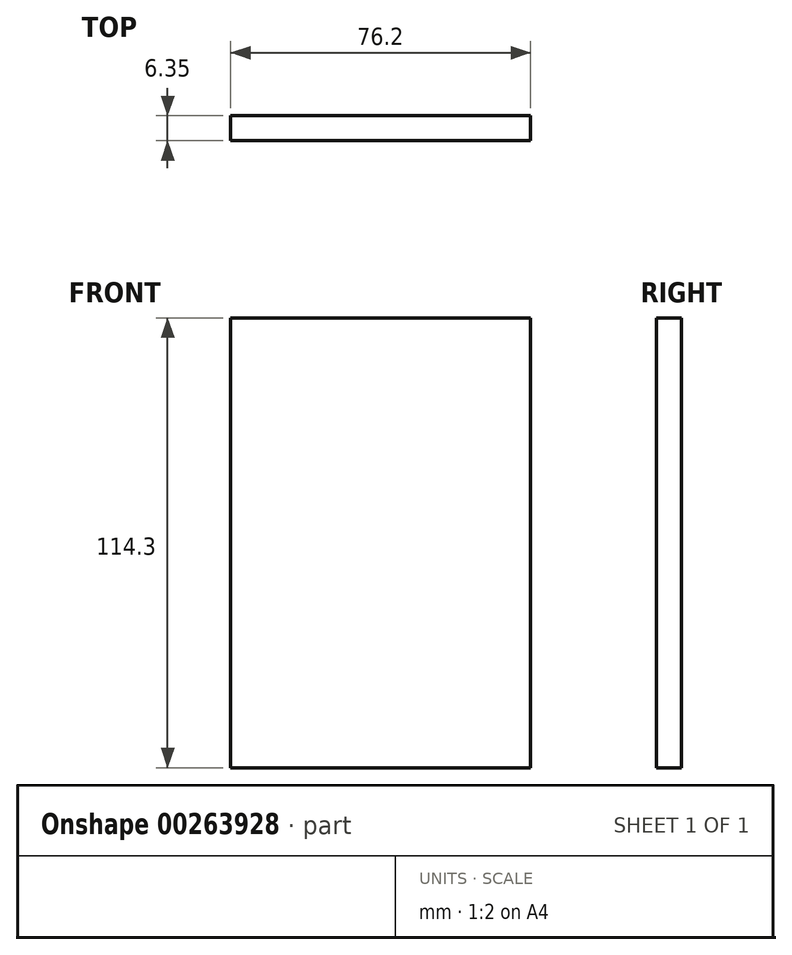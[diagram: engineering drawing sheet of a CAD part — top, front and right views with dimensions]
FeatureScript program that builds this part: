
annotation { "Feature Type Name" : "Feature", "Feature Type Description" : "" }
export const myFeature = defineFeature(function(context is Context, id is Id, definition is map)
    precondition{}
    {
        {
            var Q0;
            Q0=qCreatedBy(makeId("Front.planeOp"),FACE);
            var sketch = newSketch(context, id + "F0", { "sketchPlane" : qUnion([Q0])});
            skLineSegment(sketch, "E0.bottom", {"start": v(38.1, 57.15) * mm, "end": v(-38.1, 57.15) * mm});
            skLineSegment(sketch, "E0.top", {"start": v(38.1, -57.15) * mm, "end": v(-38.1, -57.15) * mm});
            skLineSegment(sketch, "E0.left", {"start": v(38.1, 57.15) * mm, "end": v(38.1, -57.15) * mm});
            skLineSegment(sketch, "E0.right", {"start": v(-38.1, 57.15) * mm, "end": v(-38.1, -57.15) * mm});
            skPoint(sketch, "E0.middle", {"position": v(0, 0) * mm});
            skSolve(sketch);
        }
        {
            var Q0;
            Q0=makeQuery(id+"F0.imprint","IMPRINT",FACE,{"disambiguationData":[TD([[makeQuery(id+"F0.imprint","IMPRINT",EDGE,{"derivedFrom":sQuery(id+"F0.wireOp",EDGE,"E0.bottom")}),1.0]])]});
            extrude(context, id + "F1", {"entities" : qUnion([Q0]), "depth" : 6.35 * mm});
        }
    });
